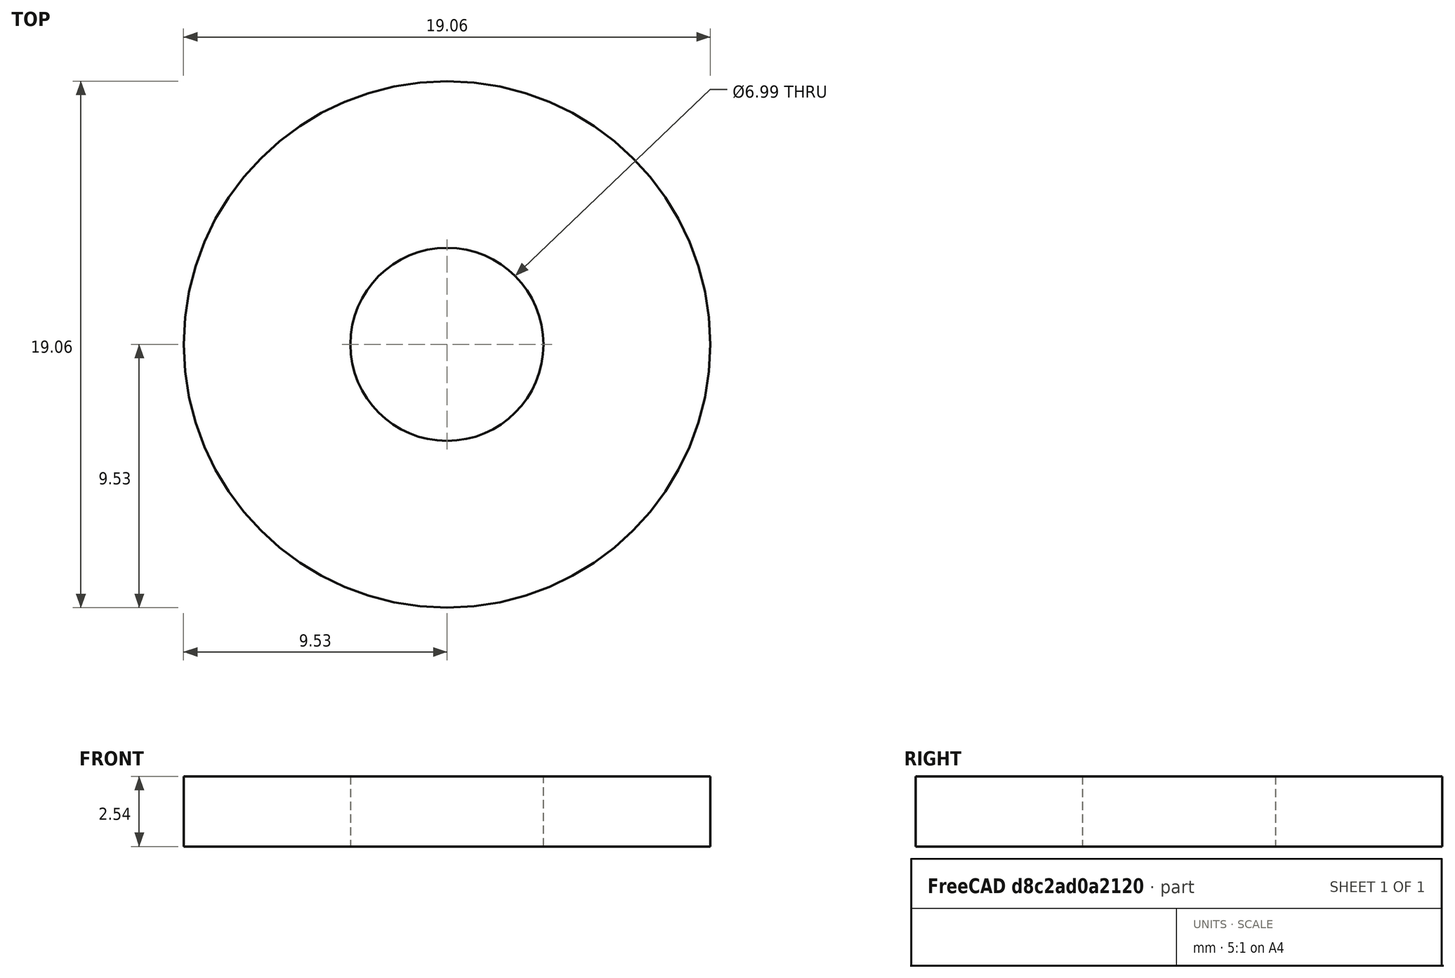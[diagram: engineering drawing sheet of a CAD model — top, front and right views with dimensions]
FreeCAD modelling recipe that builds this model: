
FCSTD DOCUMENT  (FreeCAD 0.22R36784 (Git))
Label: linux panel washers
License: All rights reserved
LicenseURL: http://en.wikipedia.org/wiki/All_rights_reserved
objects: Sketcher::SketchObject×1, PartDesign::Pad×1, PartDesign::Body×1
note: 4 computed .brp shape members not serialized (recipe doc carries the construction recipe); baked Part::Feature solids carry a one-line shape summary decoded from their .brp

FEATURE [Sketcher::SketchObject] Sketch
  AttachmentSupport = -> [XY_Plane]
  FullyConstrained = true
  MapMode = 5
  sketch-geometry (2):
    g0: Circle CenterX=0 CenterY=0 CenterZ=0 NormalX=0 NormalY=0 NormalZ=1 AngleXU=0 Radius=9.525
    g1: Circle CenterX=0 CenterY=0 CenterZ=0 NormalX=0 NormalY=0 NormalZ=1 AngleXU=0 Radius=3.4925
  constraints (4):
    c: Coincident(g0,g-1)
    c: Coincident(g1,g0)
    c: Diameter(g1) = 6.985
    c: Diameter(g0) = 19.05
FEATURE [PartDesign::Pad] Pad
  Direction = (0,0,1)
  Length = 2.54
  Length2 = 10
  Profile = -> Sketch
  ReferenceAxis = -> Sketch [N_Axis]
  Suppressed = false
  Type = 0
FEATURE [PartDesign::Body] Body
  Group = -> [Sketch,Pad]
  Origin = -> Origin
  Tip = -> Pad
